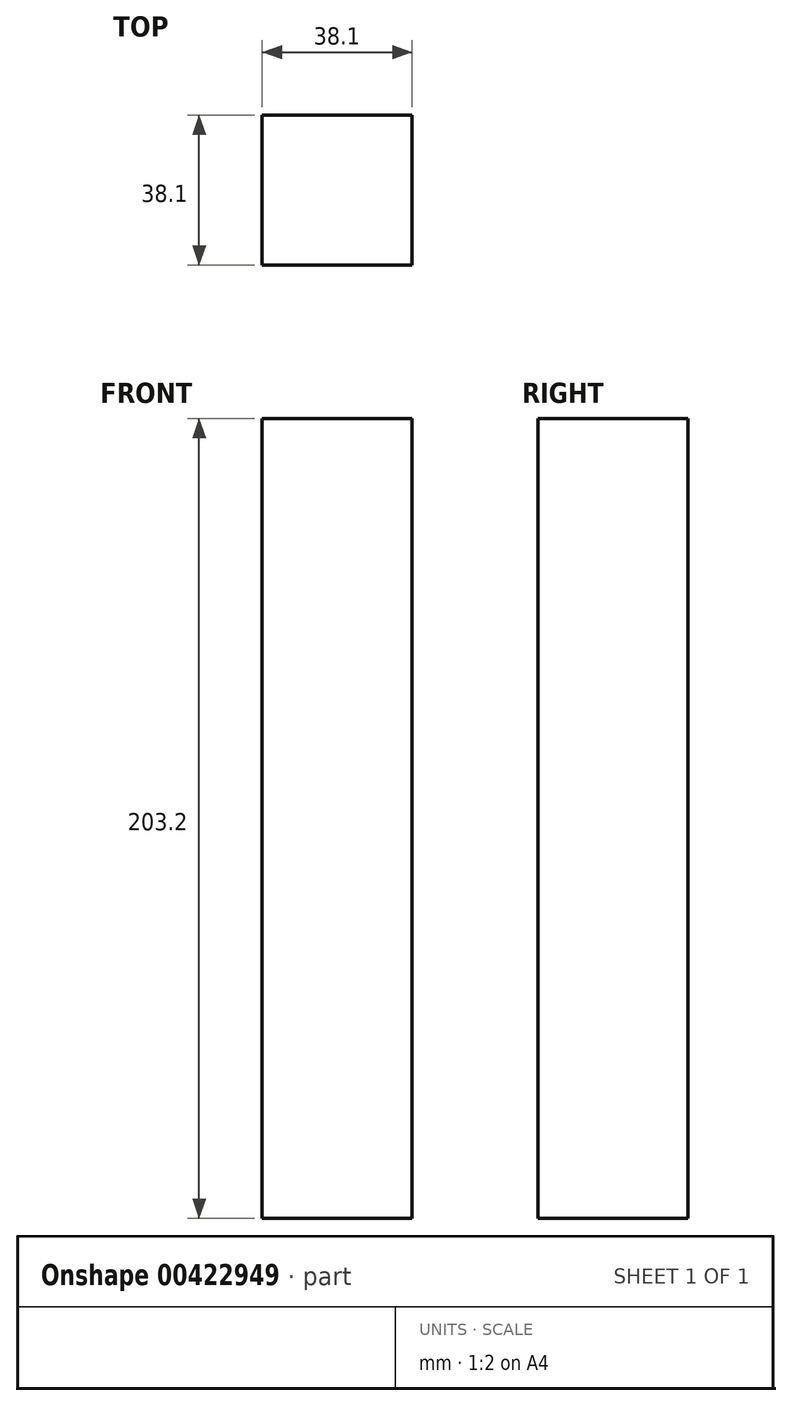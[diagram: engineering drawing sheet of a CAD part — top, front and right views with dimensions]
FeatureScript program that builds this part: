
annotation { "Feature Type Name" : "Feature", "Feature Type Description" : "" }
export const myFeature = defineFeature(function(context is Context, id is Id, definition is map)
    precondition{}
    {
        {
            var Q0;
            Q0=qCreatedBy(makeId("Top.planeOp"),FACE);
            var sketch = newSketch(context, id + "F0", { "sketchPlane" : qUnion([Q0])});
            skLineSegment(sketch, "E0.bottom", {"start": v(19.05, 19.05) * mm, "end": v(-19.05, 19.05) * mm});
            skLineSegment(sketch, "E0.top", {"start": v(19.05, -19.05) * mm, "end": v(-19.05, -19.05) * mm});
            skLineSegment(sketch, "E0.left", {"start": v(19.05, 19.05) * mm, "end": v(19.05, -19.05) * mm});
            skLineSegment(sketch, "E0.right", {"start": v(-19.05, 19.05) * mm, "end": v(-19.05, -19.05) * mm});
            skPoint(sketch, "E0.middle", {"position": v(0, 0) * mm});
            skSolve(sketch);
        }
        {
            var Q0;
            Q0 = qSketchRegion(id + "F0", true);
            extrude(context, id + "F1", {"entities" : qUnion([Q0]), "depth" : 203.2 * mm, "offsetDistance" : 25.4 * mm});
        }
    });
